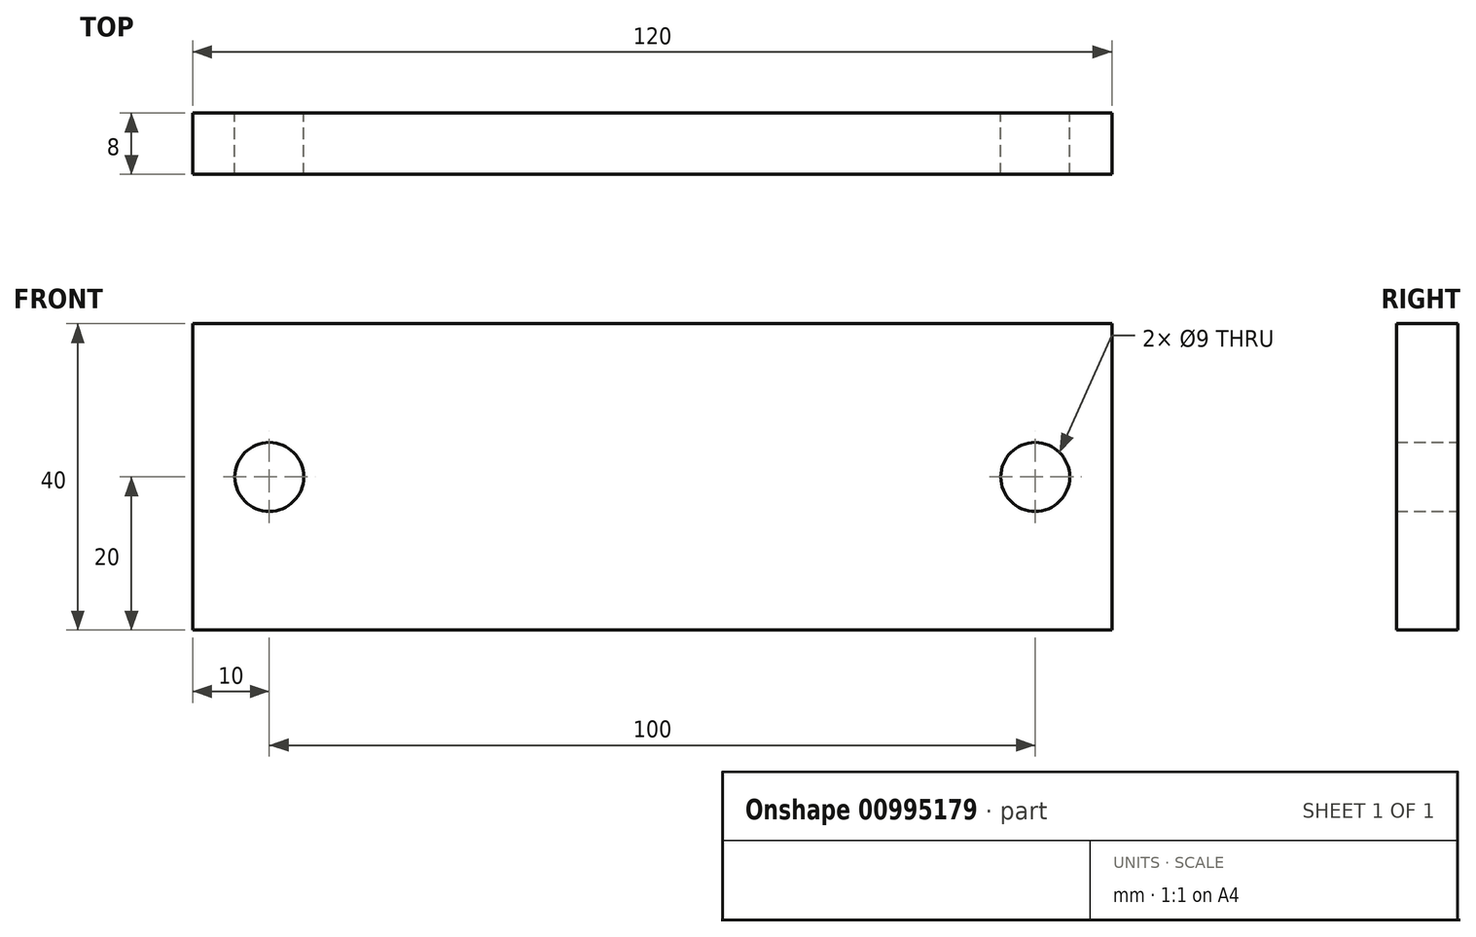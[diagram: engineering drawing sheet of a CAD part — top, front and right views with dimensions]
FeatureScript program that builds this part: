
annotation { "Feature Type Name" : "Feature", "Feature Type Description" : "" }
export const myFeature = defineFeature(function(context is Context, id is Id, definition is map)
    precondition{}
    {
        {
            var Q0;
            Q0=qCreatedBy(makeId("Front.planeOp"),FACE);
            var sketch = newSketch(context, id + "F0", { "sketchPlane" : qUnion([Q0])});
            skLineSegment(sketch, "E0.bottom", {"start": v(-60, 20) * mm, "end": v(60, 20) * mm});
            skLineSegment(sketch, "E0.top", {"start": v(-60, -20) * mm, "end": v(60, -20) * mm});
            skLineSegment(sketch, "E0.left", {"start": v(-60, 20) * mm, "end": v(-60, -20) * mm});
            skLineSegment(sketch, "E0.right", {"start": v(60, 20) * mm, "end": v(60, -20) * mm});
            skPoint(sketch, "E0.middle", {"position": v(0, 0) * mm});
            skSolve(sketch);
        }
        {
            var Q0;
            Q0=makeQuery(id+"F0.imprint","IMPRINT",FACE,{"disambiguationData":[TD([[makeQuery(id+"F0.imprint","IMPRINT",EDGE,{"derivedFrom":sQuery(id+"F0.wireOp",EDGE,"E0.bottom")}),-1.0]])]});
            extrude(context, id + "F1", {"entities" : qUnion([Q0]), "depth" : 8 * mm, "offsetDistance" : 25 * mm, "symmetric" : true});
        }
        {
            var Q0;
            Q0=makeQuery(id+"F1.opExtrude","CAP_FACE",FACE,{"disambiguationData":[OSD([sQuery(id+"F0.wireOp",EDGE,"E0.bottom"),sQuery(id+"F0.wireOp",EDGE,"E0.top"),sQuery(id+"F0.wireOp",EDGE,"E0.left"),sQuery(id+"F0.wireOp",EDGE,"E0.right")])],"isStart":false});
            var sketch = newSketch(context, id + "F2", { "sketchPlane" : qUnion([Q0])});
            skLineSegment(sketch, "E1", {"start": v(0, 0) * mm, "end": v(-50, 0) * mm});
            skLineSegment(sketch, "E2", {"start": v(0, 0) * mm, "end": v(50, 0) * mm});
            skSolve(sketch);
        }
        {
            var Q0;
            Q0=sQuery(id+"F2.wireOp",VERTEX,"E1.end");
            var Q1;
            Q1=sQuery(id+"F2.wireOp",VERTEX,"E2.end");
            var Q2;
            Q2=makeQuery(id+"F1.opExtrude","SWEPT_BODY",BODY,{"disambiguationData":[OSD([sQuery(id+"F0.wireOp",EDGE,"E0.bottom"),sQuery(id+"F0.wireOp",EDGE,"E0.top"),sQuery(id+"F0.wireOp",EDGE,"E0.left"),sQuery(id+"F0.wireOp",EDGE,"E0.right")])]});
            hole(context, id + "F3", {"style" : HoleStyle.SIMPLE, "endStyle" : HoleEndStyle.THROUGH, "holeDiameter" : 9 * mm, "majorDiameter" : 5 * mm, "isTappedThrough" : true, "tappedDepth" : 12 * mm, "tapClearance" : 3, "locations" : qUnion([Q0, Q1]), "scope" : qUnion([Q2]), "startStyle" : HoleStartStyle.PART});
        }
    });
